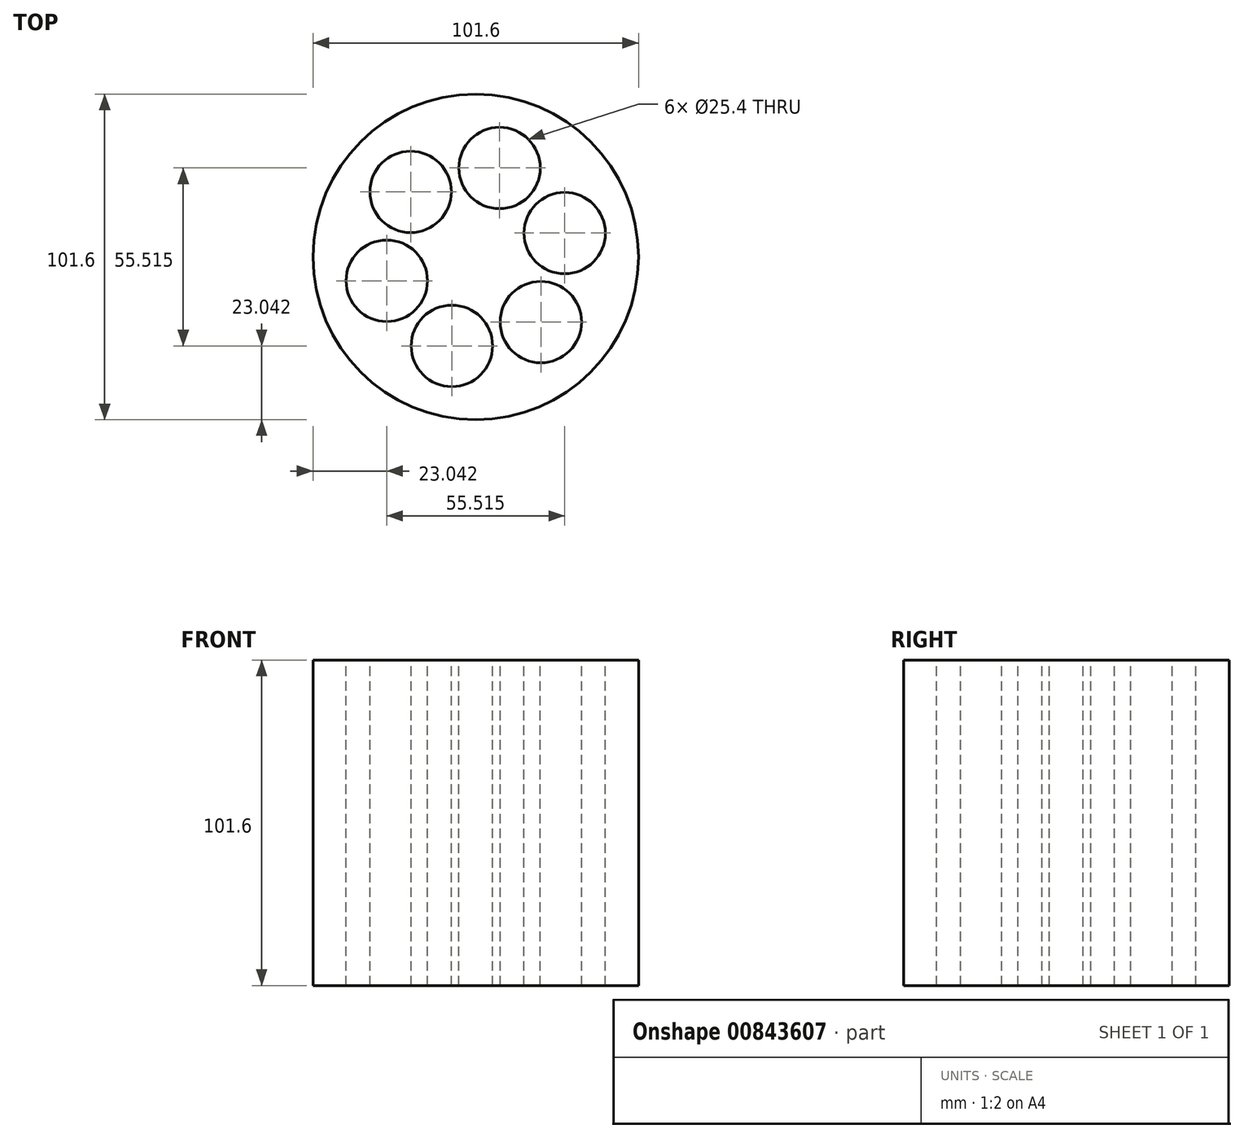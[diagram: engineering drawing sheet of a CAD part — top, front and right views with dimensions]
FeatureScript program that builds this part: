
annotation { "Feature Type Name" : "Feature", "Feature Type Description" : "" }
export const myFeature = defineFeature(function(context is Context, id is Id, definition is map)
    precondition{}
    {
        {
            var Q0;
            Q0=qCreatedBy(makeId("Top.planeOp"),FACE);
            var sketch = newSketch(context, id + "F0", { "sketchPlane" : qUnion([Q0])});
            skCircle(sketch, "E0", {"center": v(0, 0) * mm, "radius": 50.8 * mm});
            skSolve(sketch);
        }
        {
            var Q0;
            Q0 = qSketchRegion(id + "F0", true);
            extrude(context, id + "F1", {"entities" : qUnion([Q0]), "depth" : 101.6 * mm, "offsetDistance" : 25.4 * mm});
        }
        {
            var Q0;
            Q0=makeQuery(id+"F1.opExtrude","CAP_FACE",FACE,{"disambiguationData":[OSD([sQuery(id+"F0.wireOp",EDGE,"E0")])],"isStart":false});
            var sketch = newSketch(context, id + "F2", { "sketchPlane" : qUnion([Q0])});
            skCircle(sketch, "E1", {"center": v(-20.32, 20.32) * mm, "radius": 12.7 * mm});
            skSolve(sketch);
        }
        {
            var Q0;
            Q0 = qSketchRegion(id + "F2", true);
            extrude(context, id + "F3", {"entities" : qUnion([Q0]), "operationType" : NewBodyOperationType.REMOVE, "endBound" : BoundingType.THROUGH_ALL, "oppositeDirection" : true, "depth" : 25.4 * mm, "offsetDistance" : 25.4 * mm});
        }
        {
            var Q0;
            Q0=qCreatedBy(makeId("Right.planeOp"),FACE);
            var sketch = newSketch(context, id + "F4", { "sketchPlane" : qUnion([Q0])});
            skLineSegment(sketch, "E2", {"start": v(0, 0) * mm, "end": v(0, 101.6) * mm});
            skSolve(sketch);
        }
        {
            var Q0;
            Q0=makeQuery(id+"F1.opExtrude","SWEPT_BODY",BODY,{"disambiguationData":[OSD([sQuery(id+"F0.wireOp",EDGE,"E0")])]});
            var Q1;
            Q1=sQuery(id+"F4.wireOp",EDGE,"E2");
            circularPattern(context, id + "F5", {"entities" : qUnion([Q0]), "axis" : qUnion([Q1]), "angle" : 360 * degree, "instanceCount" : 6, "equalSpace" : true});
        }
    });
